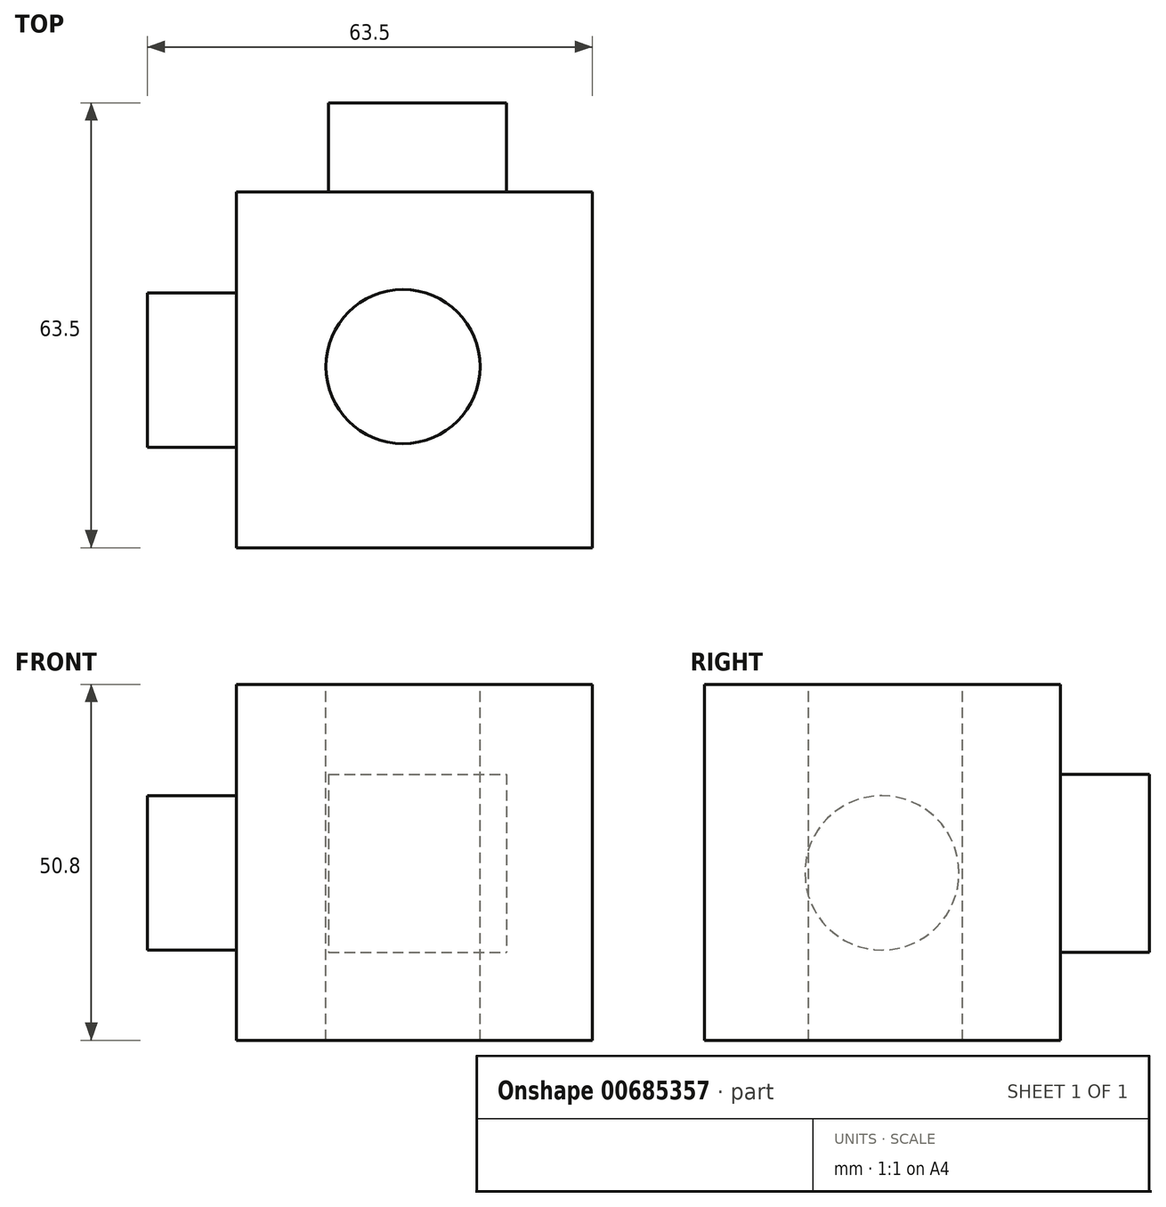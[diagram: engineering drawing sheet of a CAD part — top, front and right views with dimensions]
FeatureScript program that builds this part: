
annotation { "Feature Type Name" : "Feature", "Feature Type Description" : "" }
export const myFeature = defineFeature(function(context is Context, id is Id, definition is map)
    precondition{}
    {
        {
            var Q0;
            Q0=qCreatedBy(makeId("Front.planeOp"),FACE);
            var sketch = newSketch(context, id + "F0", { "sketchPlane" : qUnion([Q0])});
            skLineSegment(sketch, "E0.bottom", {"start": v(5, 26.9) * mm, "end": v(55.8, 26.9) * mm});
            skLineSegment(sketch, "E0.top", {"start": v(5, -23.9) * mm, "end": v(55.8, -23.9) * mm});
            skLineSegment(sketch, "E0.left", {"start": v(5, 26.9) * mm, "end": v(5, -23.9) * mm});
            skLineSegment(sketch, "E0.right", {"start": v(55.8, 26.9) * mm, "end": v(55.8, -23.9) * mm});
            skSolve(sketch);
        }
        {
            var Q0;
            Q0=makeQuery(id+"F0.imprint","IMPRINT",FACE,{"disambiguationData":[TD([[makeQuery(id+"F0.imprint","IMPRINT",EDGE,{"derivedFrom":sQuery(id+"F0.wireOp",EDGE,"E0.bottom")}),-1.0]])]});
            extrude(context, id + "F1", {"entities" : qUnion([Q0]), "depth" : 50.8 * mm, "offsetDistance" : 25.4 * mm});
        }
        {
            var Q0;
            Q0=qCreatedBy(makeId("Front.planeOp"),FACE);
            var sketch = newSketch(context, id + "F2", { "sketchPlane" : qUnion([Q0])});
            skLineSegment(sketch, "E1.bottom", {"start": v(18.14, 14.08) * mm, "end": v(43.54, 14.08) * mm});
            skLineSegment(sketch, "E1.top", {"start": v(18.14, -11.32) * mm, "end": v(43.54, -11.32) * mm});
            skLineSegment(sketch, "E1.left", {"start": v(18.14, 14.08) * mm, "end": v(18.14, -11.32) * mm});
            skLineSegment(sketch, "E1.right", {"start": v(43.54, 14.08) * mm, "end": v(43.54, -11.32) * mm});
            skSolve(sketch);
        }
        {
            var Q0;
            Q0=makeQuery(id+"F2.imprint","IMPRINT",FACE,{"disambiguationData":[TD([[makeQuery(id+"F2.imprint","IMPRINT",EDGE,{"derivedFrom":sQuery(id+"F2.wireOp",EDGE,"E1.bottom")}),-1.0]])]});
            var sketch = newSketch(context, id + "F3", { "sketchPlane" : qUnion([Q0])});
            skSolve(sketch);
        }
        {
            var Q0;
            Q0 = qSketchRegion(id + "F3", true);
            var Q1;
            Q1=makeQuery(id+"F2.imprint","IMPRINT",FACE,{"disambiguationData":[TD([[makeQuery(id+"F2.imprint","IMPRINT",EDGE,{"derivedFrom":sQuery(id+"F2.wireOp",EDGE,"E1.bottom")}),-1.0]])]});
            extrude(context, id + "F4", {"entities" : qUnion([Q0, Q1]), "oppositeDirection" : true, "depth" : 12.7 * mm, "offsetDistance" : 25.4 * mm});
        }
        {
            var Q0;
            Q0=makeQuery(id+"FBuaQPbuP1BcNV7_2.imprint","IMPRINT",FACE,{"disambiguationData":[TD([[makeQuery(id+"FBuaQPbuP1BcNV7_2.imprint","IMPRINT",EDGE,{"derivedFrom":sQuery(id+"FBuaQPbuP1BcNV7_2.wireOp",EDGE,"WGBkdF5q-tJn5-Mghr-orNR-mOjjKjK6F4ZY")}),1.0]])]});
            var sketch = newSketch(context, id + "F5", { "sketchPlane" : qUnion([Q0])});
            skSolve(sketch);
        }
        {
            var Q0;
            Q0=makeQuery(id+"F1.opExtrude","SWEPT_FACE",FACE,{"disambiguationData":[OSD([sQuery(id+"F0.wireOp",EDGE,"E0.left")])]});
            var sketch = newSketch(context, id + "F6", { "sketchPlane" : qUnion([Q0])});
            skCircle(sketch, "E2", {"center": v(25.47, 0) * mm, "radius": 11 * mm});
            skSolve(sketch);
        }
        {
            var Q0;
            Q0 = qSketchRegion(id + "F6", true);
            var Q1;
            Q1=makeQuery(id+"F5.imprint","IMPRINT",FACE,{"disambiguationData":[TD([[makeQuery(id+"F5.imprint","IMPRINT",EDGE,{"derivedFrom":makeQuery(id+"FBuaQPbuP1BcNV7_2.imprint","IMPRINT",EDGE,{"derivedFrom":sQuery(id+"FBuaQPbuP1BcNV7_2.wireOp",EDGE,"WGBkdF5q-tJn5-Mghr-orNR-mOjjKjK6F4ZY")})}),1.0]])]});
            extrude(context, id + "F7", {"entities" : qUnion([Q0, Q1]), "operationType" : NewBodyOperationType.ADD, "depth" : 12.7 * mm, "offsetDistance" : 25.4 * mm});
        }
        {
            var Q0;
            Q0=makeQuery(id+"F1.opExtrude","SWEPT_FACE",FACE,{"disambiguationData":[OSD([sQuery(id+"F0.wireOp",EDGE,"E0.bottom")])]});
            var sketch = newSketch(context, id + "F8", { "sketchPlane" : qUnion([Q0])});
            skCircle(sketch, "E3", {"center": v(28.77, -24.95) * mm, "radius": 11 * mm});
            skSolve(sketch);
        }
        {
            var Q0;
            Q0 = qSketchRegion(id + "F8", true);
            extrude(context, id + "F9", {"entities" : qUnion([Q0]), "operationType" : NewBodyOperationType.REMOVE, "oppositeDirection" : true, "depth" : 50.8 * mm, "offsetDistance" : 25.4 * mm});
        }
    });
